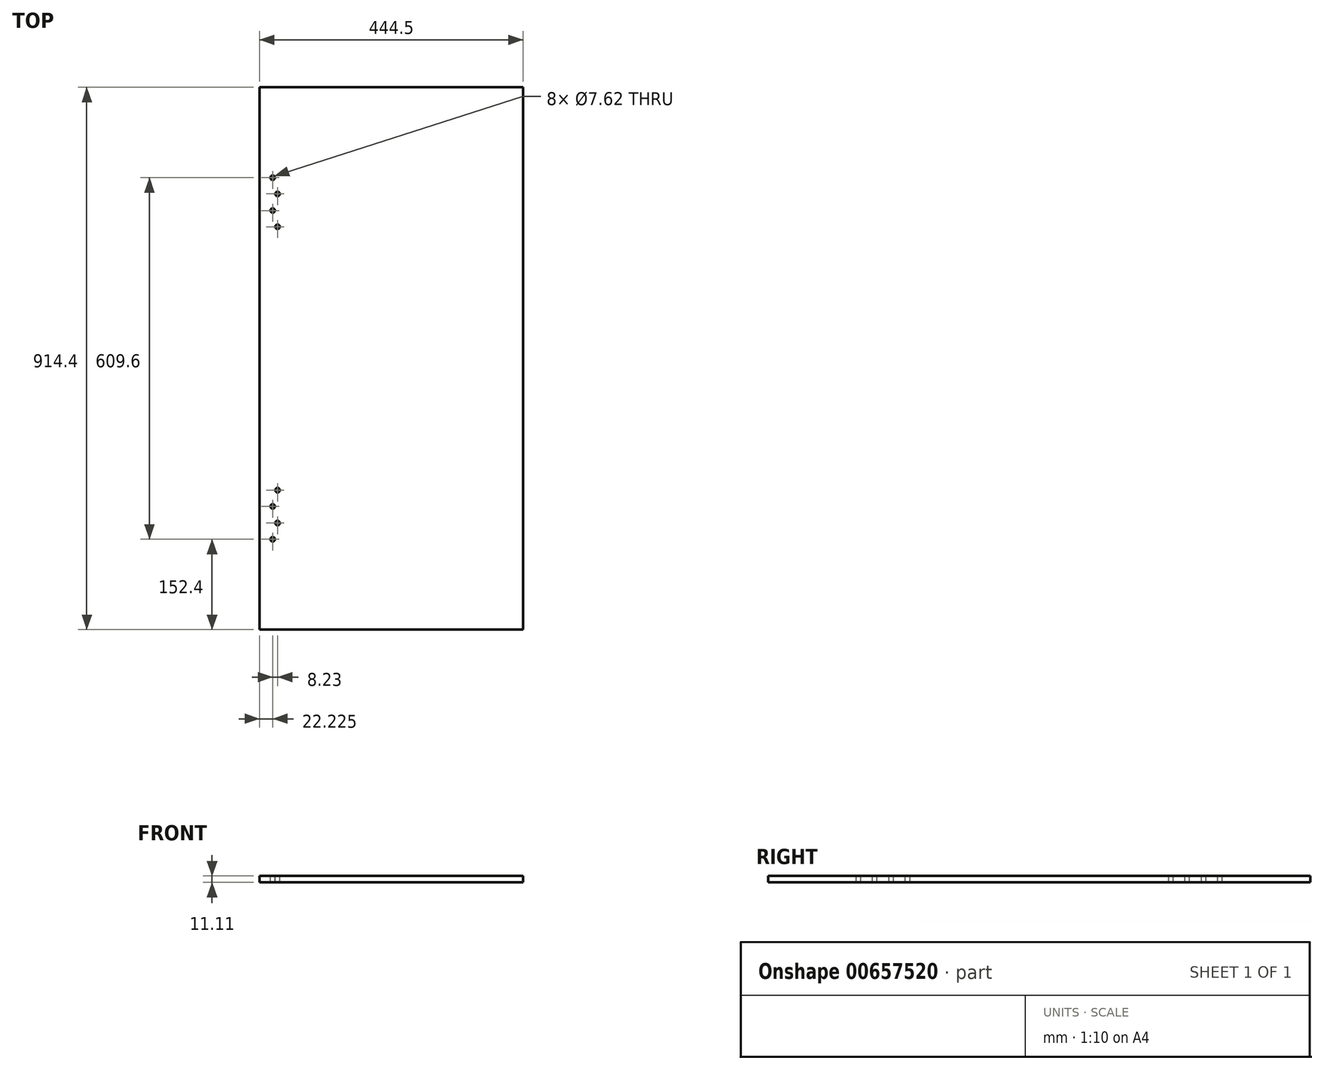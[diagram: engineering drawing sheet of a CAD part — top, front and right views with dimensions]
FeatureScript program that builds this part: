
annotation { "Feature Type Name" : "Feature", "Feature Type Description" : "" }
export const myFeature = defineFeature(function(context is Context, id is Id, definition is map)
    precondition{}
    {
        {
            var Q0;
            Q0=qCreatedBy(makeId("Top.planeOp"),FACE);
            var sketch = newSketch(context, id + "F0", { "sketchPlane" : qUnion([Q0])});
            skLineSegment(sketch, "E0.bottom", {"start": v(-222.25, 457.2) * mm, "end": v(222.25, 457.2) * mm});
            skLineSegment(sketch, "E0.top", {"start": v(-222.25, -457.2) * mm, "end": v(222.25, -457.2) * mm});
            skLineSegment(sketch, "E0.left", {"start": v(-222.25, 457.2) * mm, "end": v(-222.25, -457.2) * mm});
            skLineSegment(sketch, "E0.right", {"start": v(222.25, 457.2) * mm, "end": v(222.25, -457.2) * mm});
            skSolve(sketch);
        }
        {
            var Q0;
            Q0 = qSketchRegion(id + "F0", true);
            extrude(context, id + "F1", {"entities" : qUnion([Q0]), "depth" : 11.1 * mm, "offsetDistance" : 25.4 * mm});
        }
        {
            var Q0;
            Q0=makeQuery(id+"F1.opExtrude","CAP_FACE",FACE,{"disambiguationData":[OSD([sQuery(id+"F0.wireOp",EDGE,"E0.bottom"),sQuery(id+"F0.wireOp",EDGE,"E0.top"),sQuery(id+"F0.wireOp",EDGE,"E0.left"),sQuery(id+"F0.wireOp",EDGE,"E0.right")])],"isStart":false});
            var sketch = newSketch(context, id + "F2", { "sketchPlane" : qUnion([Q0])});
            skPoint(sketch, "E1", {"position": v(-200.02, 304.8) * mm});
            skPoint(sketch, "E2", {"position": v(-191.8, 277.44) * mm});
            skPoint(sketch, "E3", {"position": v(-200.02, 249.42) * mm});
            skPoint(sketch, "E4", {"position": v(-191.8, 222.06) * mm});
            skPoint(sketch, "E5", {"position": v(-200.02, -304.8) * mm});
            skPoint(sketch, "E6", {"position": v(-200.02, -249.42) * mm});
            skPoint(sketch, "E7", {"position": v(-191.8, -277.44) * mm});
            skPoint(sketch, "E8", {"position": v(-191.8, -222.06) * mm});
            skSolve(sketch);
        }
        {
            var Q0;
            Q0=sQuery(id+"F2.wireOp",VERTEX,"E2");
            var Q1;
            Q1=sQuery(id+"F2.wireOp",VERTEX,"E1");
            var Q2;
            Q2=sQuery(id+"F2.wireOp",VERTEX,"E3");
            var Q3;
            Q3=sQuery(id+"F2.wireOp",VERTEX,"E4");
            var Q4;
            Q4=sQuery(id+"F2.wireOp",VERTEX,"E8");
            var Q5;
            Q5=sQuery(id+"F2.wireOp",VERTEX,"E6");
            var Q6;
            Q6=sQuery(id+"F2.wireOp",VERTEX,"E7");
            var Q7;
            Q7=sQuery(id+"F2.wireOp",VERTEX,"E5");
            var Q8;
            Q8=makeQuery(id+"F1.opExtrude","SWEPT_BODY",BODY,{"disambiguationData":[OSD([sQuery(id+"F0.wireOp",EDGE,"E0.bottom"),sQuery(id+"F0.wireOp",EDGE,"E0.top"),sQuery(id+"F0.wireOp",EDGE,"E0.left"),sQuery(id+"F0.wireOp",EDGE,"E0.right")])]});
            hole(context, id + "F3", {"style" : HoleStyle.SIMPLE, "endStyle" : HoleEndStyle.BLIND, "holeDiameter" : 7.62 * mm, "majorDiameter" : 6.35 * mm, "holeDepth" : 12.7 * mm, "isTappedThrough" : true, "tappedDepth" : 12.7 * mm, "tapClearance" : 3, "locations" : qUnion([Q0, Q1, Q2, Q3, Q4, Q5, Q6, Q7]), "scope" : qUnion([Q8])});
        }
    });
